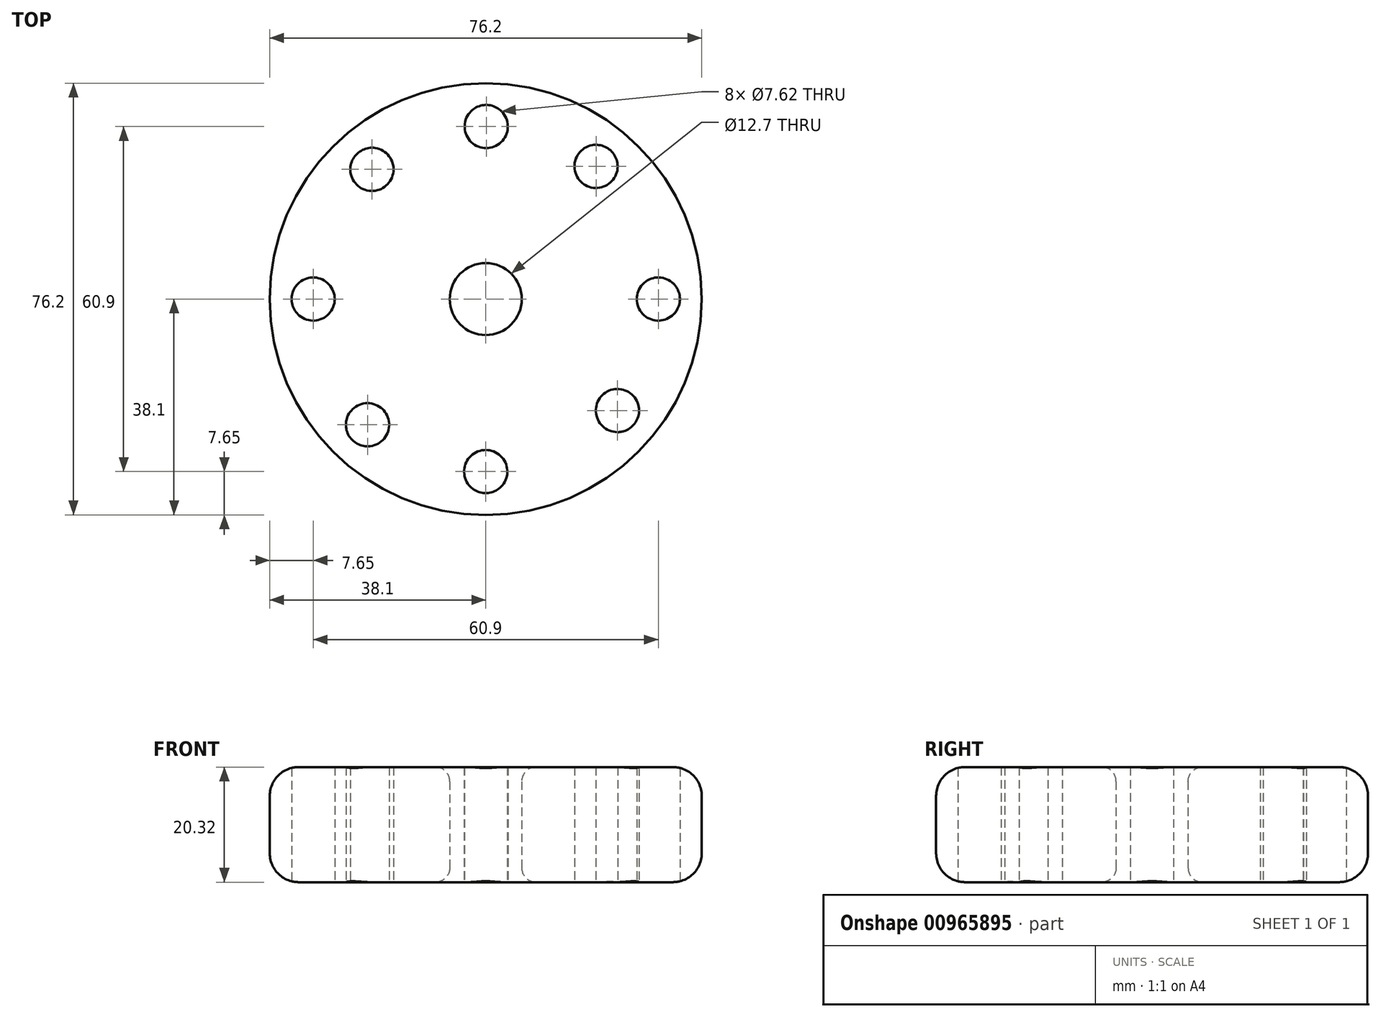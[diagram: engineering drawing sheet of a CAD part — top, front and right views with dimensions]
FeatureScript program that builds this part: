
annotation { "Feature Type Name" : "Feature", "Feature Type Description" : "" }
export const myFeature = defineFeature(function(context is Context, id is Id, definition is map)
    precondition{}
    {
        {
            var Q0;
            Q0=qCreatedBy(makeId("Top.planeOp"),FACE);
            var sketch = newSketch(context, id + "F0", { "sketchPlane" : qUnion([Q0])});
            skCircle(sketch, "E0", {"center": v(0, 0) * mm, "radius": 38.1 * mm});
            skCircle(sketch, "E1", {"center": v(-30.45, 0) * mm, "radius": 3.81 * mm});
            skCircle(sketch, "E2", {"center": v(-20.08, 22.9) * mm, "radius": 3.81 * mm});
            skCircle(sketch, "E3", {"center": v(0.1, 30.45) * mm, "radius": 3.81 * mm});
            skCircle(sketch, "E4", {"center": v(19.47, 23.41) * mm, "radius": 3.81 * mm});
            skCircle(sketch, "E5", {"center": v(30.45, 0) * mm, "radius": 3.81 * mm});
            skCircle(sketch, "E6", {"center": v(23.24, -19.67) * mm, "radius": 3.81 * mm});
            skCircle(sketch, "E7", {"center": v(0, -30.45) * mm, "radius": 3.81 * mm});
            skCircle(sketch, "E8", {"center": v(-20.86, -22.18) * mm, "radius": 3.81 * mm});
            skArc(sketch, "E9.trimOffspring", {"start": v(-3.8, -30.21) * mm, "mid": v(0, -30.45) * mm, "end": v(3.8, -30.21) * mm});
            skArc(sketch, "E10.trimOffspring", {"start": v(-23.46, -19.4) * mm, "mid": v(-20.86, -22.18) * mm, "end": v(-17.92, -24.62) * mm});
            skCircle(sketch, "E11", {"center": v(0, 0) * mm, "radius": 6.35 * mm});
            skSolve(sketch);
        }
        {
            var Q0;
            Q0=makeQuery(id+"F0.imprint","IMPRINT",FACE,{"disambiguationData":[TD([[makeQuery(id+"F0.imprint","IMPRINT",EDGE,{"derivedFrom":sQuery(id+"F0.wireOp",EDGE,"E0")}),1.0]])]});
            extrude(context, id + "F1", {"entities" : qUnion([Q0]), "depth" : 20.32 * mm, "offsetDistance" : 25.4 * mm});
        }
        {
            var Q0;
            Q0=makeQuery(id+"F1.opExtrude","CAP_EDGE",EDGE,{"disambiguationData":[OSD([sQuery(id+"F0.wireOp",EDGE,"E0")])],"isStart":false});
            var Q1;
            Q1=makeQuery(id+"F1.opExtrude","CAP_EDGE",EDGE,{"disambiguationData":[OSD([sQuery(id+"F0.wireOp",EDGE,"E0")])],"isStart":true});
            fillet(context, id + "F2", {"entities" : qUnion([Q0, Q1]), "radius" : 5.08 * mm, "tangentPropagation" : true, "allowEdgeOverflow" : false});
        }
        {
            var Q0;
            Q0=makeQuery(id+"F1.opExtrude","SWEPT_FACE",FACE,{"disambiguationData":[OSD([sQuery(id+"F0.wireOp",EDGE,"E11")])]});
            fillet(context, id + "F3", {"entities" : qUnion([Q0]), "radius" : 2.54 * mm, "tangentPropagation" : true, "allowEdgeOverflow" : false});
        }
    });
